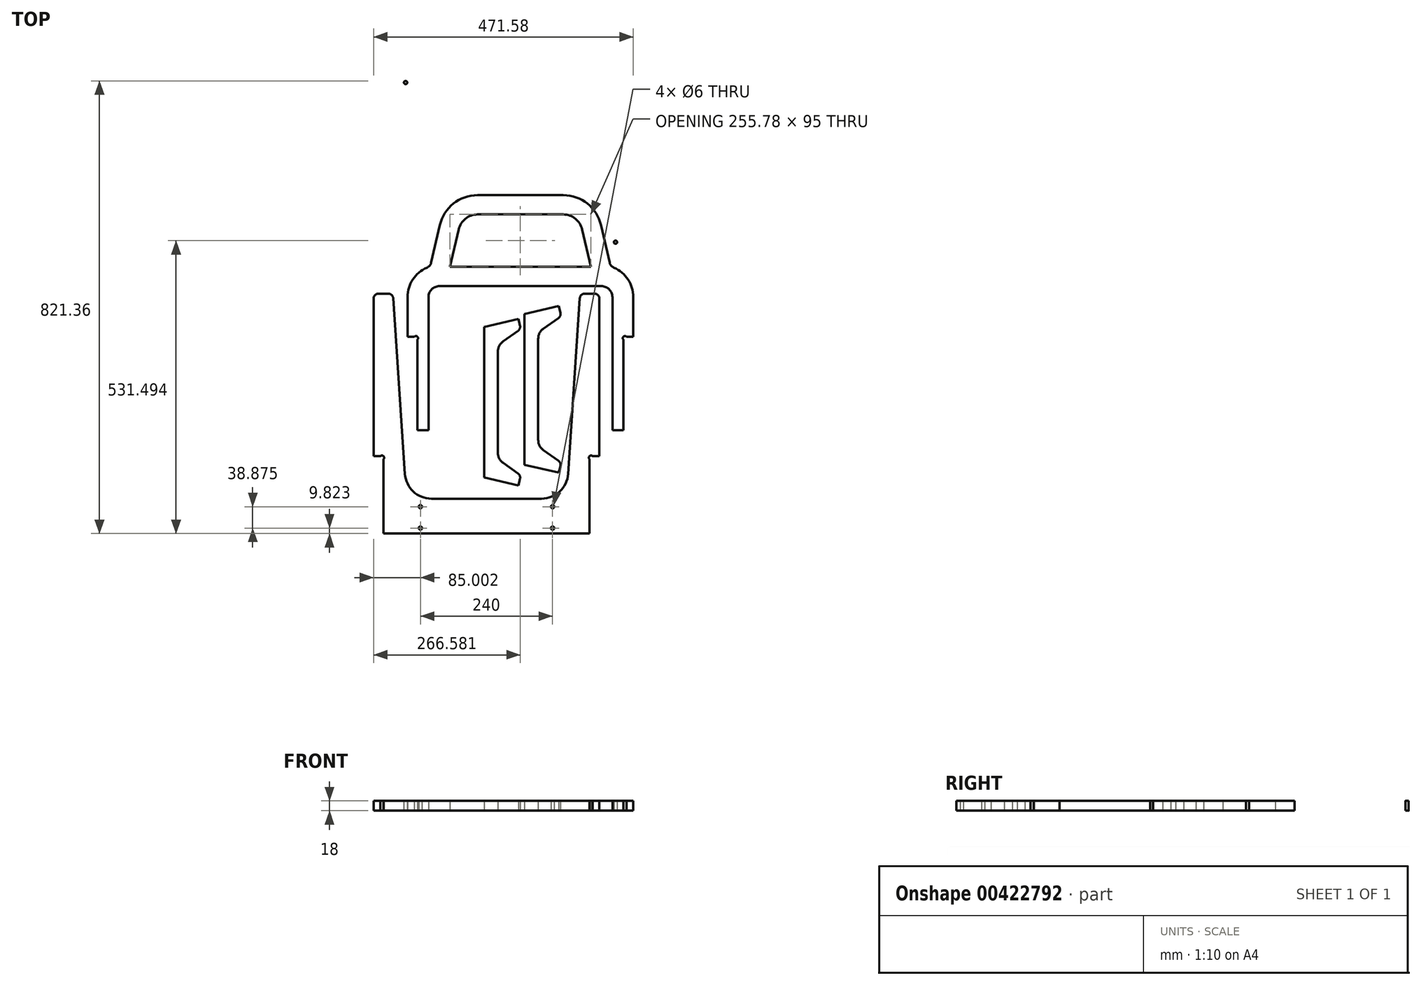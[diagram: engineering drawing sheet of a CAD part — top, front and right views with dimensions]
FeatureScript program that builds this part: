
annotation { "Feature Type Name" : "Feature", "Feature Type Description" : "" }
export const myFeature = defineFeature(function(context is Context, id is Id, definition is map)
    precondition{}
    {
        {
            var Q0;
            Q0=qCreatedBy(makeId("Top.planeOp"),FACE);
            var sketch = newSketch(context, id + "F0", { "sketchPlane" : qUnion([Q0])});
            skCircle(sketch, "E0", {"center": v(529.27, 111.7) * mm, "radius": 3 * mm});
            skCircle(sketch, "E1", {"center": v(514.14, 177.27) * mm, "radius": 3 * mm});
            skCircle(sketch, "E2", {"center": v(524.1, 361.94) * mm, "radius": 3 * mm});
            skCircle(sketch, "E3", {"center": v(445.74, 237.09) * mm, "radius": 3 * mm});
            skCircle(sketch, "E4", {"center": v(234.56, 237.09) * mm, "radius": 3 * mm});
            skCircle(sketch, "E5", {"center": v(199.38, 177.27) * mm, "radius": 3 * mm});
            skCircle(sketch, "E6", {"center": v(184.24, 111.7) * mm, "radius": 3 * mm});
            skCircle(sketch, "E7", {"center": v(504.8, 294.59) * mm, "radius": 3 * mm});
            skArc(sketch, "E8", {"start": v(222.05, 246.59) * mm, "mid": v(209.6, 242.24) * mm, "end": v(202.57, 231.09) * mm});
            skLineSegment(sketch, "E9", {"start": v(222.05, 246.59) * mm, "end": v(451.52, 246.59) * mm});
            skArc(sketch, "E10", {"start": v(451.52, 246.59) * mm, "mid": v(475.6, 254.64) * mm, "end": v(489.97, 275.56) * mm});
            skLineSegment(sketch, "E11", {"start": v(489.97, 275.56) * mm, "end": v(521.1, 384.1) * mm});
            skLineSegment(sketch, "E12", {"start": v(521.1, 384.1) * mm, "end": v(538.4, 379.14) * mm});
            skLineSegment(sketch, "E13", {"start": v(538.4, 379.14) * mm, "end": v(514.95, 297.37) * mm});
            skArc(sketch, "E14", {"start": v(514.95, 297.37) * mm, "mid": v(509.2, 259.95) * mm, "end": v(512.98, 222.28) * mm});
            skLineSegment(sketch, "E15", {"start": v(512.98, 222.28) * mm, "end": v(543.24, 91.23) * mm});
            skLineSegment(sketch, "E16", {"start": v(543.24, 91.23) * mm, "end": v(525.7, 87.18) * mm});
            skLineSegment(sketch, "E17", {"start": v(525.7, 87.18) * mm, "end": v(512.45, 144.59) * mm});
            skArc(sketch, "E18", {"start": v(512.45, 144.59) * mm, "mid": v(484.3, 189.2) * mm, "end": v(434.5, 206.59) * mm});
            skLineSegment(sketch, "E19", {"start": v(434.5, 206.59) * mm, "end": v(279.02, 206.59) * mm});
            skArc(sketch, "E20", {"start": v(279.02, 206.59) * mm, "mid": v(229.22, 189.2) * mm, "end": v(201.07, 144.59) * mm});
            skLineSegment(sketch, "E21", {"start": v(201.07, 144.59) * mm, "end": v(187.08, 83.97) * mm});
            skLineSegment(sketch, "E22", {"start": v(187.08, 83.97) * mm, "end": v(169.54, 88.02) * mm});
            skLineSegment(sketch, "E23", {"start": v(169.54, 88.02) * mm, "end": v(202.57, 231.09) * mm});
            skLineSegment(sketch, "E24", {"start": v(210.21, 142.47) * mm, "end": v(194.52, 74.52) * mm});
            skLineSegment(sketch, "E25", {"start": v(518.72, 74.52) * mm, "end": v(503.03, 142.47) * mm});
            skArc(sketch, "E26", {"start": v(468.93, 134.6) * mm, "mid": v(456.44, 154.38) * mm, "end": v(434.36, 162.1) * mm});
            skLineSegment(sketch, "E27", {"start": v(434.36, 162.1) * mm, "end": v(278.88, 162.1) * mm});
            skArc(sketch, "E28", {"start": v(278.88, 162.1) * mm, "mid": v(256.8, 154.38) * mm, "end": v(244.32, 134.6) * mm});
            skArc(sketch, "E29", {"start": v(503.03, 142.47) * mm, "mid": v(478.23, 181.77) * mm, "end": v(434.36, 197.1) * mm});
            skLineSegment(sketch, "E30", {"start": v(434.36, 197.1) * mm, "end": v(278.88, 197.1) * mm});
            skArc(sketch, "E31", {"start": v(278.88, 197.1) * mm, "mid": v(235, 181.77) * mm, "end": v(210.21, 142.47) * mm});
            skLineSegment(sketch, "E32", {"start": v(169.62, -229.18) * mm, "end": v(189.62, -229.18) * mm});
            skLineSegment(sketch, "E33", {"start": v(189.62, -229.18) * mm, "end": v(189.62, 12.1) * mm});
            skArc(sketch, "E34", {"start": v(209.62, 32.1) * mm, "mid": v(195.48, 26.24) * mm, "end": v(189.62, 12.1) * mm});
            skLineSegment(sketch, "E35", {"start": v(209.62, 32.1) * mm, "end": v(503.62, 32.1) * mm});
            skArc(sketch, "E36", {"start": v(523.62, 12.1) * mm, "mid": v(517.76, 26.24) * mm, "end": v(503.62, 32.1) * mm});
            skLineSegment(sketch, "E37", {"start": v(523.62, 12.1) * mm, "end": v(523.62, -229.18) * mm});
            skLineSegment(sketch, "E38", {"start": v(523.62, -229.18) * mm, "end": v(543.62, -229.18) * mm});
            skLineSegment(sketch, "E39", {"start": v(543.62, -229.18) * mm, "end": v(543.62, -65.27) * mm});
            skArc(sketch, "E40", {"start": v(549.28, -59.61) * mm, "mid": v(543.62, -59.61) * mm, "end": v(543.62, -65.27) * mm});
            skLineSegment(sketch, "E41", {"start": v(549.28, -59.61) * mm, "end": v(561.62, -59.61) * mm});
            skLineSegment(sketch, "E42", {"start": v(151.62, -59.61) * mm, "end": v(163.96, -59.61) * mm});
            skArc(sketch, "E43", {"start": v(169.62, -65.27) * mm, "mid": v(169.62, -59.61) * mm, "end": v(163.96, -59.61) * mm});
            skLineSegment(sketch, "E44", {"start": v(169.62, -65.27) * mm, "end": v(169.62, -229.18) * mm});
            skLineSegment(sketch, "E45", {"start": v(468.93, 134.6) * mm, "end": v(484.51, 67.1) * mm});
            skLineSegment(sketch, "E46", {"start": v(484.51, 67.1) * mm, "end": v(228.73, 67.1) * mm});
            skLineSegment(sketch, "E47", {"start": v(228.73, 67.1) * mm, "end": v(244.32, 134.6) * mm});
            skArc(sketch, "E48", {"start": v(561.62, 12.1) * mm, "mid": v(552, 44.1) * mm, "end": v(526.3, 65.48) * mm});
            skLineSegment(sketch, "E49", {"start": v(561.62, 12.1) * mm, "end": v(561.62, -59.61) * mm});
            skArc(sketch, "E50", {"start": v(518.72, 74.52) * mm, "mid": v(521.42, 69.09) * mm, "end": v(526.3, 65.48) * mm});
            skArc(sketch, "E51", {"start": v(186.94, 65.48) * mm, "mid": v(161.25, 44.1) * mm, "end": v(151.62, 12.1) * mm});
            skArc(sketch, "E52", {"start": v(186.94, 65.48) * mm, "mid": v(191.82, 69.09) * mm, "end": v(194.52, 74.52) * mm});
            skLineSegment(sketch, "E53", {"start": v(151.62, 12.1) * mm, "end": v(151.62, -59.61) * mm});
            skLineSegment(sketch, "E54", {"start": v(194.07, 114.28) * mm, "end": v(203.35, 112.14) * mm});
            skLineSegment(sketch, "E55", {"start": v(356.76, 206.59) * mm, "end": v(356.76, 197.06) * mm});
            skLineSegment(sketch, "E56", {"start": v(519.07, 115.88) * mm, "end": v(509.8, 113.74) * mm});
            skCircle(sketch, "E57", {"center": v(148.12, 401.46) * mm, "radius": 3 * mm});
            skCircle(sketch, "E58", {"center": v(163.26, 335.9) * mm, "radius": 3 * mm});
            skCircle(sketch, "E59", {"center": v(153.3, 151.23) * mm, "radius": 3 * mm});
            skCircle(sketch, "E60", {"center": v(231.65, 276.07) * mm, "radius": 3 * mm});
            skCircle(sketch, "E61", {"center": v(442.84, 276.07) * mm, "radius": 3 * mm});
            skCircle(sketch, "E62", {"center": v(478.02, 335.9) * mm, "radius": 3 * mm});
            skCircle(sketch, "E63", {"center": v(493.16, 401.46) * mm, "radius": 3 * mm});
            skCircle(sketch, "E64", {"center": v(172.6, 218.58) * mm, "radius": 3 * mm});
            skArc(sketch, "E65", {"start": v(455.34, 266.57) * mm, "mid": v(467.8, 270.92) * mm, "end": v(474.83, 282.08) * mm});
            skLineSegment(sketch, "E66", {"start": v(455.34, 266.57) * mm, "end": v(225.88, 266.57) * mm});
            skArc(sketch, "E67", {"start": v(225.88, 266.57) * mm, "mid": v(201.8, 258.52) * mm, "end": v(187.42, 237.6) * mm});
            skLineSegment(sketch, "E68", {"start": v(187.42, 237.6) * mm, "end": v(156.3, 129.06) * mm});
            skLineSegment(sketch, "E69", {"start": v(156.3, 129.06) * mm, "end": v(139, 134.02) * mm});
            skLineSegment(sketch, "E70", {"start": v(139, 134.02) * mm, "end": v(162.45, 215.8) * mm});
            skArc(sketch, "E71", {"start": v(162.45, 215.8) * mm, "mid": v(168.2, 253.22) * mm, "end": v(164.41, 290.89) * mm});
            skLineSegment(sketch, "E72", {"start": v(164.41, 290.89) * mm, "end": v(134.16, 421.93) * mm});
            skLineSegment(sketch, "E73", {"start": v(134.16, 421.93) * mm, "end": v(151.7, 425.98) * mm});
            skLineSegment(sketch, "E74", {"start": v(151.7, 425.98) * mm, "end": v(164.95, 368.58) * mm});
            skArc(sketch, "E75", {"start": v(164.95, 368.58) * mm, "mid": v(193.1, 323.97) * mm, "end": v(242.9, 306.57) * mm});
            skLineSegment(sketch, "E76", {"start": v(242.9, 306.57) * mm, "end": v(398.38, 306.57) * mm});
            skArc(sketch, "E77", {"start": v(398.38, 306.57) * mm, "mid": v(448.18, 323.97) * mm, "end": v(476.33, 368.58) * mm});
            skLineSegment(sketch, "E78", {"start": v(476.33, 368.58) * mm, "end": v(490.32, 429.2) * mm});
            skLineSegment(sketch, "E79", {"start": v(490.32, 429.2) * mm, "end": v(507.86, 425.14) * mm});
            skLineSegment(sketch, "E80", {"start": v(507.86, 425.14) * mm, "end": v(474.83, 282.08) * mm});
            skLineSegment(sketch, "E81", {"start": v(483.33, 398.88) * mm, "end": v(474.04, 401.03) * mm});
            skLineSegment(sketch, "E82", {"start": v(320.64, 306.57) * mm, "end": v(320.64, 316.1) * mm});
            skLineSegment(sketch, "E83", {"start": v(158.32, 397.28) * mm, "end": v(167.6, 399.42) * mm});
            skLineSegment(sketch, "E84", {"start": v(363.94, -18.72) * mm, "end": v(363.94, -292.03) * mm});
            skLineSegment(sketch, "E85", {"start": v(363.94, -292.03) * mm, "end": v(426.45, -306.46) * mm});
            skLineSegment(sketch, "E86", {"start": v(426.45, -306.46) * mm, "end": v(429.2, -294.53) * mm});
            skArc(sketch, "E87", {"start": v(429.2, -294.53) * mm, "mid": v(428.82, -289.07) * mm, "end": v(425.47, -284.74) * mm});
            skLineSegment(sketch, "E88", {"start": v(425.47, -284.74) * mm, "end": v(398.36, -265.56) * mm});
            skArc(sketch, "E89", {"start": v(398.36, -265.56) * mm, "mid": v(391.44, -257.6) * mm, "end": v(388.94, -247.37) * mm});
            skLineSegment(sketch, "E90", {"start": v(388.94, -247.37) * mm, "end": v(388.94, -63.38) * mm});
            skArc(sketch, "E91", {"start": v(388.94, -63.38) * mm, "mid": v(391.44, -53.13) * mm, "end": v(398.36, -45.18) * mm});
            skLineSegment(sketch, "E92", {"start": v(398.36, -45.18) * mm, "end": v(425.47, -26) * mm});
            skArc(sketch, "E93", {"start": v(425.47, -26) * mm, "mid": v(428.82, -21.67) * mm, "end": v(429.2, -16.2) * mm});
            skLineSegment(sketch, "E94", {"start": v(429.2, -16.2) * mm, "end": v(426.45, -4.29) * mm});
            skLineSegment(sketch, "E95", {"start": v(426.45, -4.29) * mm, "end": v(363.94, -18.72) * mm});
            skArc(sketch, "E96", {"start": v(500.04, 9.5) * mm, "mid": v(497.4, 15.86) * mm, "end": v(491.04, 18.5) * mm});
            skLineSegment(sketch, "E97", {"start": v(491.04, 18.5) * mm, "end": v(473.46, 18.5) * mm});
            skArc(sketch, "E98", {"start": v(473.46, 18.5) * mm, "mid": v(467.31, 16.07) * mm, "end": v(464.48, 10.1) * mm});
            skLineSegment(sketch, "E99", {"start": v(464.48, 10.1) * mm, "end": v(443.23, -308.5) * mm});
            skArc(sketch, "E100", {"start": v(443.23, -308.5) * mm, "mid": v(428.01, -340.6) * mm, "end": v(394.97, -353.65) * mm});
            skLineSegment(sketch, "E101", {"start": v(394.97, -353.65) * mm, "end": v(295.04, -353.65) * mm});
            skLineSegment(sketch, "E102", {"start": v(295.04, -353.65) * mm, "end": v(195.11, -353.65) * mm});
            skArc(sketch, "E103", {"start": v(195.11, -353.65) * mm, "mid": v(162.07, -340.6) * mm, "end": v(146.85, -308.5) * mm});
            skLineSegment(sketch, "E104", {"start": v(146.85, -308.5) * mm, "end": v(125.6, 10.1) * mm});
            skArc(sketch, "E105", {"start": v(125.6, 10.1) * mm, "mid": v(122.77, 16.07) * mm, "end": v(116.62, 18.5) * mm});
            skLineSegment(sketch, "E106", {"start": v(116.62, 18.5) * mm, "end": v(99.04, 18.5) * mm});
            skArc(sketch, "E107", {"start": v(99.04, 18.5) * mm, "mid": v(92.68, 15.86) * mm, "end": v(90.04, 9.5) * mm});
            skLineSegment(sketch, "E108", {"start": v(90.04, 9.5) * mm, "end": v(90.04, -276.5) * mm});
            skLineSegment(sketch, "E109", {"start": v(90.04, -276.5) * mm, "end": v(102.38, -276.5) * mm});
            skArc(sketch, "E110", {"start": v(102.38, -276.5) * mm, "mid": v(108.04, -276.5) * mm, "end": v(108.04, -282.16) * mm});
            skLineSegment(sketch, "E111", {"start": v(108.04, -282.16) * mm, "end": v(108.04, -416.9) * mm});
            skLineSegment(sketch, "E112", {"start": v(108.04, -416.9) * mm, "end": v(482.04, -416.9) * mm});
            skLineSegment(sketch, "E113", {"start": v(482.04, -416.9) * mm, "end": v(482.04, -282.16) * mm});
            skArc(sketch, "E114", {"start": v(482.04, -282.16) * mm, "mid": v(482.04, -276.5) * mm, "end": v(487.7, -276.5) * mm});
            skLineSegment(sketch, "E115", {"start": v(487.7, -276.5) * mm, "end": v(500.04, -276.5) * mm});
            skLineSegment(sketch, "E116", {"start": v(500.04, -276.5) * mm, "end": v(500.04, 9.5) * mm});
            skCircle(sketch, "E117", {"center": v(175.04, -407.08) * mm, "radius": 3 * mm});
            skCircle(sketch, "E118", {"center": v(415.04, -368.2) * mm, "radius": 3 * mm});
            skCircle(sketch, "E119", {"center": v(415.04, -407.08) * mm, "radius": 3 * mm});
            skCircle(sketch, "E120", {"center": v(175.04, -368.2) * mm, "radius": 3 * mm});
            skArc(sketch, "E121", {"start": v(-134.27, -237.52) * mm, "mid": v(-140.43, -240.6) * mm, "end": v(-146.96, -238.41) * mm});
            skLineSegment(sketch, "E122", {"start": v(-146.96, -238.41) * mm, "end": v(-160.24, -226.89) * mm});
            skArc(sketch, "E123", {"start": v(-160.24, -226.89) * mm, "mid": v(-163.29, -221.02) * mm, "end": v(-161.5, -214.66) * mm});
            skLineSegment(sketch, "E124", {"start": v(-161.5, -214.66) * mm, "end": v(31.36, 39.82) * mm});
            skArc(sketch, "E125", {"start": v(31.36, 39.82) * mm, "mid": v(40.92, 74.04) * mm, "end": v(24.53, 105.55) * mm});
            skLineSegment(sketch, "E126", {"start": v(24.53, 105.55) * mm, "end": v(-50.92, 171.08) * mm});
            skLineSegment(sketch, "E127", {"start": v(-50.92, 171.08) * mm, "end": v(-126.37, 236.6) * mm});
            skArc(sketch, "E128", {"start": v(-126.37, 236.6) * mm, "mid": v(-159.87, 248.42) * mm, "end": v(-192.4, 234.16) * mm});
            skLineSegment(sketch, "E129", {"start": v(-192.4, 234.16) * mm, "end": v(-417.36, 7.55) * mm});
            skArc(sketch, "E130", {"start": v(-417.36, 7.55) * mm, "mid": v(-423.42, 4.9) * mm, "end": v(-429.65, 7.1) * mm});
            skLineSegment(sketch, "E131", {"start": v(-429.65, 7.1) * mm, "end": v(-442.92, 18.63) * mm});
            skArc(sketch, "E132", {"start": v(-442.92, 18.63) * mm, "mid": v(-446, 24.8) * mm, "end": v(-443.82, 31.32) * mm});
            skLineSegment(sketch, "E133", {"start": v(-443.82, 31.32) * mm, "end": v(-256.29, 247.25) * mm});
            skLineSegment(sketch, "E134", {"start": v(-256.29, 247.25) * mm, "end": v(-246.97, 239.16) * mm});
            skArc(sketch, "E135", {"start": v(-246.97, 239.16) * mm, "mid": v(-242.7, 235.45) * mm, "end": v(-238.99, 239.72) * mm});
            skLineSegment(sketch, "E136", {"start": v(-238.99, 239.72) * mm, "end": v(-150.63, 341.45) * mm});
            skLineSegment(sketch, "E137", {"start": v(-150.63, 341.45) * mm, "end": v(131.74, 96.21) * mm});
            skLineSegment(sketch, "E138", {"start": v(131.74, 96.21) * mm, "end": v(43.38, -5.52) * mm});
            skArc(sketch, "E139", {"start": v(43.38, -5.52) * mm, "mid": v(39.68, -9.8) * mm, "end": v(43.95, -13.5) * mm});
            skLineSegment(sketch, "E140", {"start": v(43.95, -13.5) * mm, "end": v(53.27, -21.6) * mm});
            skLineSegment(sketch, "E141", {"start": v(53.27, -21.6) * mm, "end": v(-134.27, -237.52) * mm});
            skCircle(sketch, "E142", {"center": v(-106.49, 290.1) * mm, "radius": 3 * mm});
            skCircle(sketch, "E143", {"center": v(49.22, 103.38) * mm, "radius": 3 * mm});
            skCircle(sketch, "E144", {"center": v(74.71, 132.73) * mm, "radius": 3 * mm});
            skCircle(sketch, "E145", {"center": v(-131.98, 260.75) * mm, "radius": 3 * mm});
            skLineSegment(sketch, "E146", {"start": v(290.68, -41.87) * mm, "end": v(290.68, -315.18) * mm});
            skLineSegment(sketch, "E147", {"start": v(290.68, -315.18) * mm, "end": v(353.18, -329.6) * mm});
            skLineSegment(sketch, "E148", {"start": v(353.18, -329.6) * mm, "end": v(355.94, -317.68) * mm});
            skArc(sketch, "E149", {"start": v(355.94, -317.68) * mm, "mid": v(355.56, -312.22) * mm, "end": v(352.2, -307.9) * mm});
            skLineSegment(sketch, "E150", {"start": v(352.2, -307.9) * mm, "end": v(325.1, -288.71) * mm});
            skArc(sketch, "E151", {"start": v(325.1, -288.71) * mm, "mid": v(318.17, -280.76) * mm, "end": v(315.68, -270.52) * mm});
            skLineSegment(sketch, "E152", {"start": v(315.68, -270.52) * mm, "end": v(315.68, -86.53) * mm});
            skArc(sketch, "E153", {"start": v(315.68, -86.53) * mm, "mid": v(318.17, -76.29) * mm, "end": v(325.1, -68.34) * mm});
            skLineSegment(sketch, "E154", {"start": v(325.1, -68.34) * mm, "end": v(352.2, -49.15) * mm});
            skArc(sketch, "E155", {"start": v(352.2, -49.15) * mm, "mid": v(355.56, -44.83) * mm, "end": v(355.94, -39.36) * mm});
            skLineSegment(sketch, "E156", {"start": v(355.94, -39.36) * mm, "end": v(353.18, -27.44) * mm});
            skLineSegment(sketch, "E157", {"start": v(353.18, -27.44) * mm, "end": v(290.68, -41.87) * mm});
            skArc(sketch, "E158", {"start": v(-208.12, -390.38) * mm, "mid": v(-206.95, -387.55) * mm, "end": v(-204.12, -386.38) * mm});
            skLineSegment(sketch, "E159", {"start": v(-204.12, -386.38) * mm, "end": v(-187.62, -386.38) * mm});
            skLineSegment(sketch, "E160", {"start": v(-187.62, -386.38) * mm, "end": v(-187.62, -79.2) * mm});
            skArc(sketch, "E161", {"start": v(-187.62, -79.2) * mm, "mid": v(-196.4, -57.98) * mm, "end": v(-217.62, -49.2) * mm});
            skLineSegment(sketch, "E162", {"start": v(-217.62, -49.2) * mm, "end": v(-531.62, -49.2) * mm});
            skArc(sketch, "E163", {"start": v(-531.62, -49.2) * mm, "mid": v(-552.83, -57.98) * mm, "end": v(-561.62, -79.2) * mm});
            skLineSegment(sketch, "E164", {"start": v(-561.62, -79.2) * mm, "end": v(-561.62, -386.38) * mm});
            skLineSegment(sketch, "E165", {"start": v(-561.62, -386.38) * mm, "end": v(-545.12, -386.38) * mm});
            skArc(sketch, "E166", {"start": v(-545.12, -386.38) * mm, "mid": v(-542.3, -387.55) * mm, "end": v(-541.12, -390.38) * mm});
            skLineSegment(sketch, "E167", {"start": v(-541.12, -390.38) * mm, "end": v(-541.12, -409.2) * mm});
            skArc(sketch, "E168", {"start": v(-541.12, -409.2) * mm, "mid": v(-535.26, -423.33) * mm, "end": v(-521.12, -429.2) * mm});
            skLineSegment(sketch, "E169", {"start": v(-521.12, -429.2) * mm, "end": v(-228.12, -429.2) * mm});
            skArc(sketch, "E170", {"start": v(-228.12, -429.2) * mm, "mid": v(-213.98, -423.33) * mm, "end": v(-208.12, -409.2) * mm});
            skLineSegment(sketch, "E171", {"start": v(-208.12, -409.2) * mm, "end": v(-208.12, -390.38) * mm});
            skSolve(sketch);
        }
        {
            var Q0;
            Q0=makeQuery(id+"F0.imprint","IMPRINT",FACE,{"disambiguationData":[TD([[makeQuery(id+"F0.imprint","IMPRINT",EDGE,{"derivedFrom":sQuery(id+"F0.wireOp",EDGE,"E158")}),1.0]])]});
            var Q1;
            Q1=makeQuery(id+"F0.imprint","IMPRINT",FACE,{"disambiguationData":[TD([[makeQuery(id+"F0.imprint","IMPRINT",EDGE,{"derivedFrom":sQuery(id+"F0.wireOp",EDGE,"E121")}),-1.0]])]});
            var Q2;
            Q2=makeQuery(id+"F0.imprint","IMPRINT",FACE,{"disambiguationData":[TD([[makeQuery(id+"F0.imprint","IMPRINT",EDGE,{"derivedFrom":sQuery(id+"F0.wireOp",EDGE,"E57")}),1.0]])]});
            var Q3;
            Q3=makeQuery(id+"F0.imprint","IMPRINT",FACE,{"disambiguationData":[TD([[makeQuery(id+"F0.imprint","IMPRINT",EDGE,{"derivedFrom":sQuery(id+"F0.wireOp",EDGE,"E0")}),1.0]])]});
            var Q4;
            Q4=makeQuery(id+"F0.imprint","IMPRINT",FACE,{"disambiguationData":[TD([[makeQuery(id+"F0.imprint","IMPRINT",EDGE,{"derivedFrom":sQuery(id+"F0.wireOp",EDGE,"E25")}),1.0]])]});
            var Q5;
            Q5=makeQuery(id+"F0.imprint","IMPRINT",FACE,{"disambiguationData":[TD([[makeQuery(id+"F0.imprint","IMPRINT",EDGE,{"derivedFrom":sQuery(id+"F0.wireOp",EDGE,"E96")}),1.0]])]});
            var Q6;
            Q6=makeQuery(id+"F0.imprint","IMPRINT",FACE,{"disambiguationData":[TD([[makeQuery(id+"F0.imprint","IMPRINT",EDGE,{"derivedFrom":sQuery(id+"F0.wireOp",EDGE,"E84")}),1.0]])]});
            var Q7;
            Q7=makeQuery(id+"F0.imprint","IMPRINT",FACE,{"disambiguationData":[TD([[makeQuery(id+"F0.imprint","IMPRINT",EDGE,{"derivedFrom":sQuery(id+"F0.wireOp",EDGE,"E146")}),1.0]])]});
            extrude(context, id + "F1", {"entities" : qUnion([Q0, Q1, Q2, Q3, Q4, Q5, Q6, Q7]), "depth" : 18 * mm});
        }
    });
